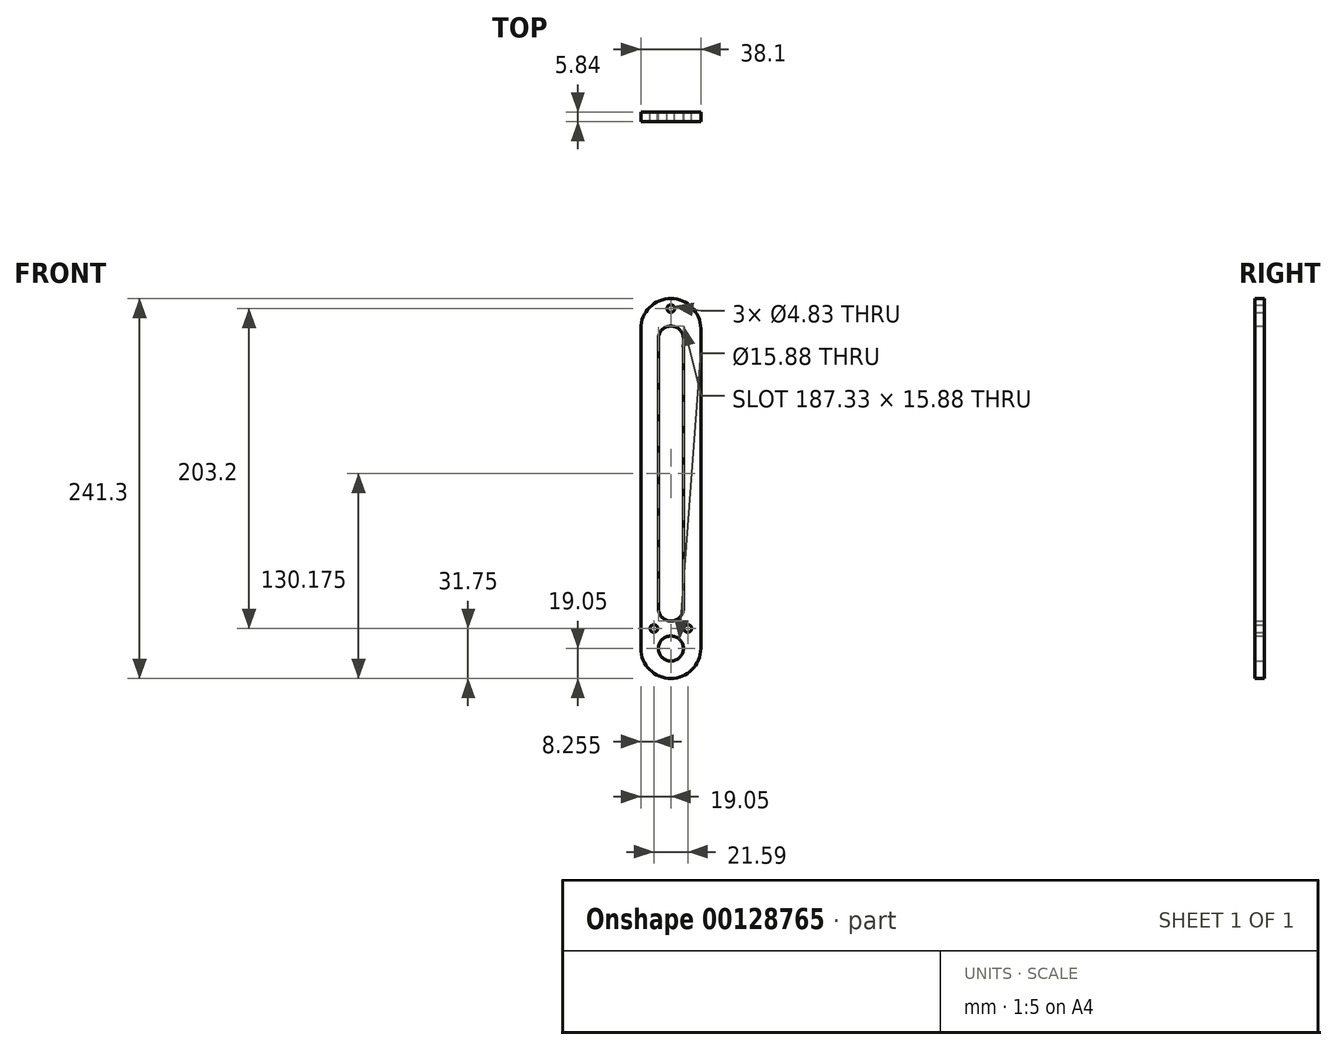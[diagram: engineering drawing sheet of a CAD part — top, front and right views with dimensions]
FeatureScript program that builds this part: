
annotation { "Feature Type Name" : "Feature", "Feature Type Description" : "" }
export const myFeature = defineFeature(function(context is Context, id is Id, definition is map)
    precondition{}
    {
        {
            var Q0;
            Q0=qCreatedBy(makeId("Front.planeOp"),FACE);
            var sketch = newSketch(context, id + "F0", { "sketchPlane" : qUnion([Q0])});
            skLineSegment(sketch, "E0", {"start": v(-19.05, -203.2) * mm, "end": v(-19.05, 0) * mm});
            skArc(sketch, "E1", {"start": v(-19.05, 0) * mm, "mid": v(0, 19.05) * mm, "end": v(19.05, 0) * mm});
            skLineSegment(sketch, "E2", {"start": v(19.05, 0) * mm, "end": v(19.05, -203.2) * mm});
            skArc(sketch, "E3", {"start": v(-19.05, -203.2) * mm, "mid": v(0, -222.25) * mm, "end": v(19.05, -203.2) * mm});
            skLineSegment(sketch, "E4", {"start": v(-7.94, -177.8) * mm, "end": v(-7.94, -6.35) * mm});
            skLineSegment(sketch, "E5", {"start": v(7.94, -177.8) * mm, "end": v(7.94, -6.35) * mm});
            skCircle(sketch, "E6", {"center": v(0, -203.2) * mm, "radius": 7.94 * mm});
            skArc(sketch, "E7", {"start": v(-7.94, -177.8) * mm, "mid": v(0, -185.74) * mm, "end": v(7.94, -177.8) * mm});
            skArc(sketch, "E8", {"start": v(-7.94, -6.35) * mm, "mid": v(0, 1.59) * mm, "end": v(7.94, -6.35) * mm});
            skCircle(sketch, "E9", {"center": v(-10.8, -190.5) * mm, "radius": 2.41 * mm});
            skCircle(sketch, "E10", {"center": v(10.8, -190.5) * mm, "radius": 2.41 * mm});
            skCircle(sketch, "E11", {"center": v(0, 12.7) * mm, "radius": 2.41 * mm});
            skSolve(sketch);
        }
        {
            var Q0;
            Q0=makeQuery(id+"F0.imprint","IMPRINT",FACE,{"disambiguationData":[TD([[makeQuery(id+"F0.imprint","IMPRINT",EDGE,{"derivedFrom":sQuery(id+"F0.wireOp",EDGE,"E0")}),-1.0]])]});
            extrude(context, id + "F1", {"entities" : qUnion([Q0]), "depth" : 5.84 * mm});
        }
    });
